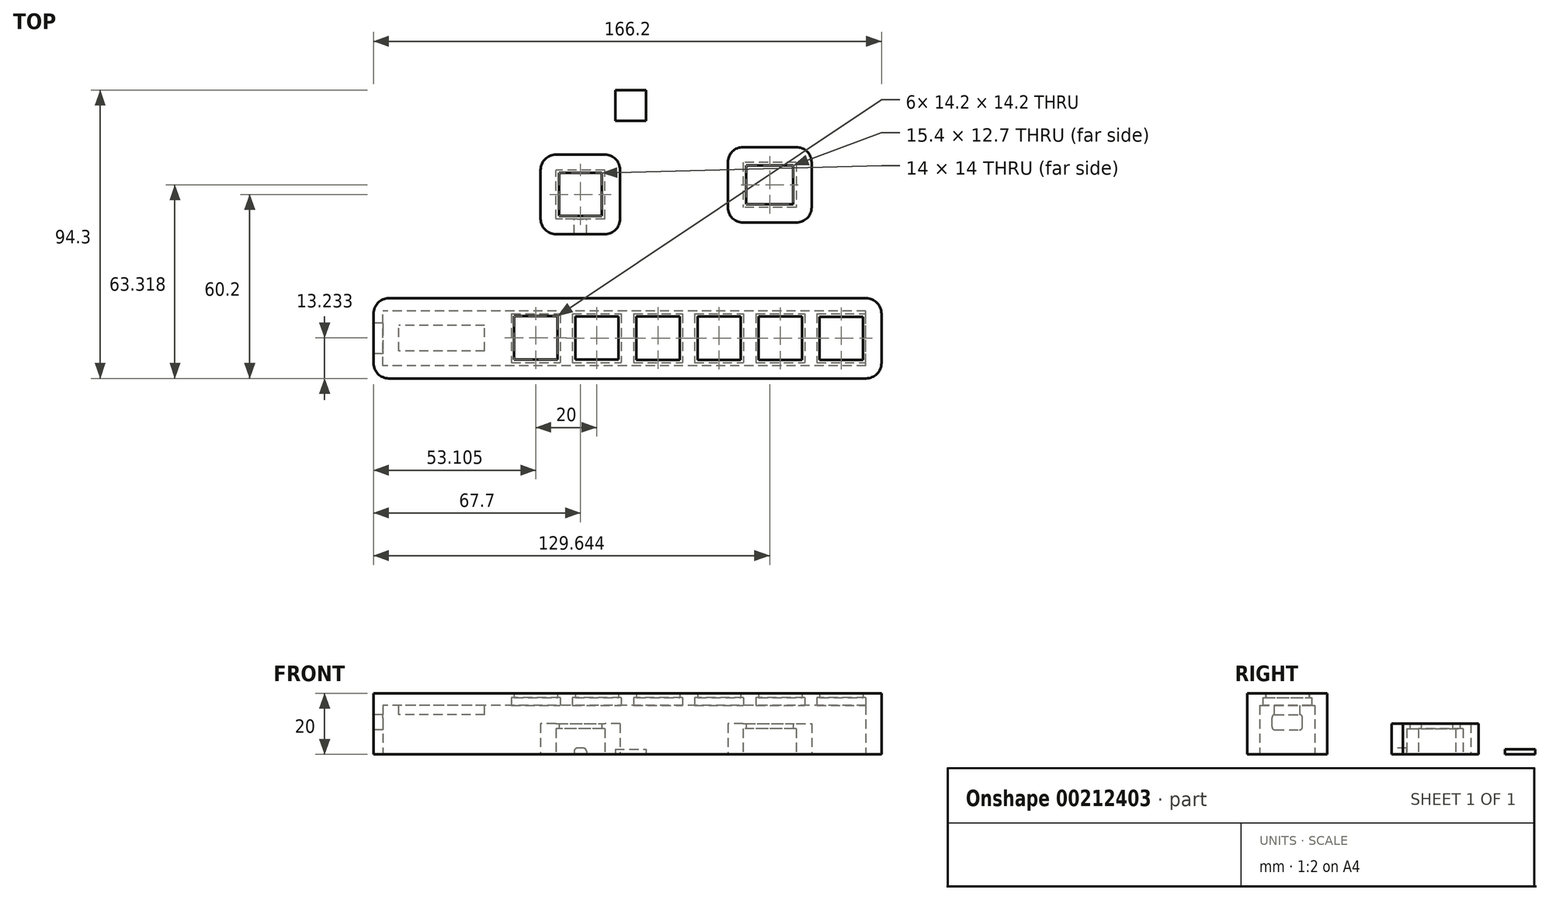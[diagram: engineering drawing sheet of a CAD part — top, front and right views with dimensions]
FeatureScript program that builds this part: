
annotation { "Feature Type Name" : "Feature", "Feature Type Description" : "" }
export const myFeature = defineFeature(function(context is Context, id is Id, definition is map)
    precondition{}
    {
        {
            var Q0;
            Q0=qCreatedBy(makeId("Top.planeOp"),FACE);
            var sketch = newSketch(context, id + "F0", { "sketchPlane" : qUnion([Q0])});
            skLineSegment(sketch, "E0.bottom", {"start": v(-7, 7) * mm, "end": v(7, 7) * mm});
            skLineSegment(sketch, "E0.top", {"start": v(-7, -7) * mm, "end": v(7, -7) * mm});
            skLineSegment(sketch, "E0.left", {"start": v(-7, 7) * mm, "end": v(-7, -7) * mm});
            skLineSegment(sketch, "E0.right", {"start": v(7, 7) * mm, "end": v(7, -7) * mm});
            skLineSegment(sketch, "E1.bottom", {"start": v(-13, 13) * mm, "end": v(13, 13) * mm});
            skLineSegment(sketch, "E1.top", {"start": v(-13, -13) * mm, "end": v(13, -13) * mm});
            skLineSegment(sketch, "E1.left", {"start": v(-13, 13) * mm, "end": v(-13, -13) * mm});
            skLineSegment(sketch, "E1.right", {"start": v(13, 13) * mm, "end": v(13, -13) * mm});
            skLineSegment(sketch, "E2.bottom", {"start": v(54.24, 9.47) * mm, "end": v(69.64, 9.47) * mm});
            skLineSegment(sketch, "E2.top", {"start": v(54.24, -3.23) * mm, "end": v(69.64, -3.23) * mm});
            skLineSegment(sketch, "E2.left", {"start": v(54.24, 9.47) * mm, "end": v(54.24, -3.23) * mm});
            skLineSegment(sketch, "E2.right", {"start": v(69.64, 9.47) * mm, "end": v(69.64, -3.23) * mm});
            skLineSegment(sketch, "E3.bottom", {"start": v(48.24, 15.47) * mm, "end": v(75.64, 15.47) * mm});
            skLineSegment(sketch, "E3.top", {"start": v(48.24, -9.23) * mm, "end": v(75.64, -9.23) * mm});
            skLineSegment(sketch, "E3.left", {"start": v(48.24, 15.47) * mm, "end": v(48.24, -9.23) * mm});
            skLineSegment(sketch, "E3.right", {"start": v(75.64, 15.47) * mm, "end": v(75.64, -9.23) * mm});
            skSolve(sketch);
        }
        {
            var Q0;
            Q0 = qSketchRegion(id + "F0", true);
            extrude(context, id + "F1", {"entities" : qUnion([Q0]), "depth" : 10 * mm});
        }
        {
            var Q0;
            Q0=makeQuery(id+"F1.opExtrude","CAP_FACE",FACE,{"disambiguationData":[OSD([sQuery(id+"F0.wireOp",EDGE,"E0.bottom"),sQuery(id+"F0.wireOp",EDGE,"E0.top"),sQuery(id+"F0.wireOp",EDGE,"E0.left"),sQuery(id+"F0.wireOp",EDGE,"E0.right"),sQuery(id+"F0.wireOp",EDGE,"E1.bottom"),sQuery(id+"F0.wireOp",EDGE,"E1.top"),sQuery(id+"F0.wireOp",EDGE,"E1.left"),sQuery(id+"F0.wireOp",EDGE,"E1.right")])],"isStart":true});
            var sketch = newSketch(context, id + "F2", { "sketchPlane" : qUnion([Q0])});
            skLineSegment(sketch, "E4.bottom", {"start": v(8, 8) * mm, "end": v(-8, 8) * mm});
            skLineSegment(sketch, "E4.top", {"start": v(8, -8) * mm, "end": v(-8, -8) * mm});
            skLineSegment(sketch, "E4.left", {"start": v(8, 8) * mm, "end": v(8, -8) * mm});
            skLineSegment(sketch, "E4.right", {"start": v(-8, 8) * mm, "end": v(-8, -8) * mm});
            skPoint(sketch, "E4.middle", {"position": v(0, 0) * mm});
            skLineSegment(sketch, "E5.bottom", {"start": v(70.64, -10.47) * mm, "end": v(53.24, -10.47) * mm});
            skLineSegment(sketch, "E5.top", {"start": v(70.64, 4.23) * mm, "end": v(53.24, 4.23) * mm});
            skLineSegment(sketch, "E5.left", {"start": v(70.64, -10.47) * mm, "end": v(70.64, 4.23) * mm});
            skLineSegment(sketch, "E5.right", {"start": v(53.24, -10.47) * mm, "end": v(53.24, 4.23) * mm});
            skSolve(sketch);
        }
        {
            var Q0;
            Q0 = qSketchRegion(id + "F2", true);
            extrude(context, id + "F3", {"entities" : qUnion([Q0]), "operationType" : NewBodyOperationType.REMOVE, "oppositeDirection" : true, "depth" : 8.4 * mm});
        }
        {
            var Q0;
            Q0=makeQuery(id+"F1.opExtrude","SWEPT_FACE",FACE,{"disambiguationData":[OSD([sQuery(id+"F0.wireOp",EDGE,"E1.top")])]});
            var sketch = newSketch(context, id + "F4", { "sketchPlane" : qUnion([Q0])});
            skLineSegment(sketch, "E6.bottom", {"start": v(2, 2) * mm, "end": v(-2, 2) * mm});
            skLineSegment(sketch, "E6.top", {"start": v(2, -2) * mm, "end": v(-2, -2) * mm});
            skLineSegment(sketch, "E6.left", {"start": v(2, 2) * mm, "end": v(2, -2) * mm});
            skLineSegment(sketch, "E6.right", {"start": v(-2, 2) * mm, "end": v(-2, -2) * mm});
            skPoint(sketch, "E6.middle", {"position": v(0, 0) * mm});
            skSolve(sketch);
        }
        {
            var Q0;
            Q0 = qSketchRegion(id + "F4", true);
            extrude(context, id + "F5", {"entities" : qUnion([Q0]), "operationType" : NewBodyOperationType.REMOVE, "endBound" : BoundingType.UP_TO_NEXT, "oppositeDirection" : true, "depth" : 25 * mm});
        }
        {
            var Q0;
            Q0=qCreatedBy(makeId("Top.planeOp"),FACE);
            var sketch = newSketch(context, id + "F6", { "sketchPlane" : qUnion([Q0])});
            skLineSegment(sketch, "E7.bottom", {"start": v(-67.7, -34) * mm, "end": v(98.5, -34) * mm});
            skLineSegment(sketch, "E7.top", {"start": v(-67.7, -60.2) * mm, "end": v(98.5, -60.2) * mm});
            skLineSegment(sketch, "E7.left", {"start": v(-67.7, -34) * mm, "end": v(-67.7, -60.2) * mm});
            skLineSegment(sketch, "E7.right", {"start": v(98.5, -34) * mm, "end": v(98.5, -60.2) * mm});
            skLineSegment(sketch, "E8", {"start": v(-67.7, -47.1) * mm, "end": v(98.5, -47.1) * mm, "construction": true});
            skLineSegment(sketch, "E9.bottom", {"start": v(92.5, -40) * mm, "end": v(78.3, -40) * mm});
            skLineSegment(sketch, "E9.top", {"start": v(92.5, -54.2) * mm, "end": v(78.3, -54.2) * mm});
            skLineSegment(sketch, "E9.left", {"start": v(92.5, -40) * mm, "end": v(92.5, -54.2) * mm});
            skLineSegment(sketch, "E9.right", {"start": v(78.3, -40) * mm, "end": v(78.3, -54.2) * mm});
            skPoint(sketch, "E9.middle", {"position": v(85.4, -47.1) * mm});
            skLineSegment(sketch, "E10.1.0.0", {"start": v(58.3, -39.98) * mm, "end": v(58.3, -54.18) * mm});
            skLineSegment(sketch, "E10.1.0.1", {"start": v(72.5, -39.98) * mm, "end": v(72.5, -54.18) * mm});
            skLineSegment(sketch, "E10.1.0.2", {"start": v(72.5, -54.18) * mm, "end": v(58.3, -54.18) * mm});
            skLineSegment(sketch, "E10.1.0.3", {"start": v(72.5, -39.98) * mm, "end": v(58.3, -39.98) * mm});
            skPoint(sketch, "E10.1.0.4", {"position": v(65.4, -47.08) * mm});
            skLineSegment(sketch, "E10.2.0.0", {"start": v(38.3, -39.95) * mm, "end": v(38.3, -54.15) * mm});
            skLineSegment(sketch, "E10.2.0.1", {"start": v(52.5, -39.95) * mm, "end": v(52.5, -54.15) * mm});
            skLineSegment(sketch, "E10.2.0.2", {"start": v(52.5, -54.15) * mm, "end": v(38.3, -54.15) * mm});
            skLineSegment(sketch, "E10.2.0.3", {"start": v(52.5, -39.95) * mm, "end": v(38.3, -39.95) * mm});
            skPoint(sketch, "E10.2.0.4", {"position": v(45.4, -47.05) * mm});
            skLineSegment(sketch, "E10.3.0.0", {"start": v(18.3, -39.92) * mm, "end": v(18.3, -54.12) * mm});
            skLineSegment(sketch, "E10.3.0.1", {"start": v(32.5, -39.92) * mm, "end": v(32.5, -54.12) * mm});
            skLineSegment(sketch, "E10.3.0.2", {"start": v(32.5, -54.12) * mm, "end": v(18.3, -54.12) * mm});
            skLineSegment(sketch, "E10.3.0.3", {"start": v(32.5, -39.92) * mm, "end": v(18.3, -39.92) * mm});
            skPoint(sketch, "E10.3.0.4", {"position": v(25.4, -47.02) * mm});
            skLineSegment(sketch, "E10.4.0.0", {"start": v(-1.7, -39.9) * mm, "end": v(-1.7, -54.1) * mm});
            skLineSegment(sketch, "E10.4.0.1", {"start": v(12.5, -39.9) * mm, "end": v(12.5, -54.1) * mm});
            skLineSegment(sketch, "E10.4.0.2", {"start": v(12.5, -54.1) * mm, "end": v(-1.7, -54.1) * mm});
            skLineSegment(sketch, "E10.4.0.3", {"start": v(12.5, -39.9) * mm, "end": v(-1.7, -39.9) * mm});
            skPoint(sketch, "E10.4.0.4", {"position": v(5.4, -47) * mm});
            skLineSegment(sketch, "E10.5.0.0", {"start": v(-21.7, -39.87) * mm, "end": v(-21.7, -54.07) * mm});
            skLineSegment(sketch, "E10.5.0.1", {"start": v(-7.5, -39.87) * mm, "end": v(-7.5, -54.07) * mm});
            skLineSegment(sketch, "E10.5.0.2", {"start": v(-7.5, -54.07) * mm, "end": v(-21.7, -54.07) * mm});
            skLineSegment(sketch, "E10.5.0.3", {"start": v(-7.5, -39.87) * mm, "end": v(-21.7, -39.87) * mm});
            skPoint(sketch, "E10.5.0.4", {"position": v(-14.6, -46.97) * mm});
            skLineSegment(sketch, "E10.direction1", {"start": v(78.3, -54.2) * mm, "end": v(58.3, -54.18) * mm, "construction": true});
            skSolve(sketch);
        }
        {
            var Q0;
            Q0 = qSketchRegion(id + "F6", true);
            extrude(context, id + "F7", {"entities" : qUnion([Q0]), "depth" : 20 * mm});
        }
        {
            var Q0;
            Q0=makeQuery(id+"F7.opExtrude","CAP_FACE",FACE,{"disambiguationData":[OSD([sQuery(id+"F6.wireOp",EDGE,"E7.bottom"),sQuery(id+"F6.wireOp",EDGE,"E7.top"),sQuery(id+"F6.wireOp",EDGE,"E7.left"),sQuery(id+"F6.wireOp",EDGE,"E7.right"),sQuery(id+"F6.wireOp",EDGE,"E9.bottom"),sQuery(id+"F6.wireOp",EDGE,"E9.top"),sQuery(id+"F6.wireOp",EDGE,"E9.left"),sQuery(id+"F6.wireOp",EDGE,"E9.right"),sQuery(id+"F6.wireOp",EDGE,"E10.1.0.0"),sQuery(id+"F6.wireOp",EDGE,"E10.1.0.1"),sQuery(id+"F6.wireOp",EDGE,"E10.1.0.2"),sQuery(id+"F6.wireOp",EDGE,"E10.1.0.3"),sQuery(id+"F6.wireOp",EDGE,"E10.2.0.0"),sQuery(id+"F6.wireOp",EDGE,"E10.2.0.1"),sQuery(id+"F6.wireOp",EDGE,"E10.2.0.2"),sQuery(id+"F6.wireOp",EDGE,"E10.2.0.3"),sQuery(id+"F6.wireOp",EDGE,"E10.3.0.0"),sQuery(id+"F6.wireOp",EDGE,"E10.3.0.1"),sQuery(id+"F6.wireOp",EDGE,"E10.3.0.2"),sQuery(id+"F6.wireOp",EDGE,"E10.3.0.3"),sQuery(id+"F6.wireOp",EDGE,"E10.4.0.0"),sQuery(id+"F6.wireOp",EDGE,"E10.4.0.1"),sQuery(id+"F6.wireOp",EDGE,"E10.4.0.2"),sQuery(id+"F6.wireOp",EDGE,"E10.4.0.3"),sQuery(id+"F6.wireOp",EDGE,"E10.5.0.0"),sQuery(id+"F6.wireOp",EDGE,"E10.5.0.1"),sQuery(id+"F6.wireOp",EDGE,"E10.5.0.2"),sQuery(id+"F6.wireOp",EDGE,"E10.5.0.3")])],"isStart":true});
            var sketch = newSketch(context, id + "F8", { "sketchPlane" : qUnion([Q0])});
            skLineSegment(sketch, "E11.bottom", {"start": v(93.4, 55.1) * mm, "end": v(77.4, 55.1) * mm});
            skLineSegment(sketch, "E11.top", {"start": v(93.4, 39.1) * mm, "end": v(77.4, 39.1) * mm});
            skLineSegment(sketch, "E11.left", {"start": v(93.4, 55.1) * mm, "end": v(93.4, 39.1) * mm});
            skLineSegment(sketch, "E11.right", {"start": v(77.4, 55.1) * mm, "end": v(77.4, 39.1) * mm});
            skPoint(sketch, "E11.middle", {"position": v(85.4, 47.1) * mm});
            skPoint(sketch, "E11.middle.positionSnap0", {"position": v(85.4, 40) * mm});
            skPoint(sketch, "E11.middle.positionSnap1", {"position": v(92.5, 47.1) * mm});
            skPoint(sketch, "E11.centerSnap0", {"position": v(85.4, 40) * mm});
            skPoint(sketch, "E11.centerSnap1", {"position": v(92.5, 47.1) * mm});
            skPoint(sketch, "E12.1.0.0", {"position": v(65.4, 40) * mm});
            skPoint(sketch, "E12.1.0.1", {"position": v(72.5, 47.1) * mm});
            skPoint(sketch, "E12.1.0.2", {"position": v(65.4, 47.1) * mm});
            skLineSegment(sketch, "E12.1.0.3", {"start": v(57.4, 55.1) * mm, "end": v(57.4, 39.1) * mm});
            skLineSegment(sketch, "E12.1.0.4", {"start": v(73.4, 55.1) * mm, "end": v(73.4, 39.1) * mm});
            skLineSegment(sketch, "E12.1.0.5", {"start": v(73.4, 39.1) * mm, "end": v(57.4, 39.1) * mm});
            skLineSegment(sketch, "E12.1.0.6", {"start": v(73.4, 55.1) * mm, "end": v(57.4, 55.1) * mm});
            skPoint(sketch, "E12.1.0.7", {"position": v(72.5, 47.1) * mm});
            skPoint(sketch, "E12.1.0.8", {"position": v(65.4, 40) * mm});
            skPoint(sketch, "E12.2.0.0", {"position": v(45.4, 40) * mm});
            skPoint(sketch, "E12.2.0.1", {"position": v(52.5, 47.1) * mm});
            skPoint(sketch, "E12.2.0.2", {"position": v(45.4, 47.1) * mm});
            skLineSegment(sketch, "E12.2.0.3", {"start": v(37.4, 55.1) * mm, "end": v(37.4, 39.1) * mm});
            skLineSegment(sketch, "E12.2.0.4", {"start": v(53.4, 55.1) * mm, "end": v(53.4, 39.1) * mm});
            skLineSegment(sketch, "E12.2.0.5", {"start": v(53.4, 39.1) * mm, "end": v(37.4, 39.1) * mm});
            skLineSegment(sketch, "E12.2.0.6", {"start": v(53.4, 55.1) * mm, "end": v(37.4, 55.1) * mm});
            skPoint(sketch, "E12.2.0.7", {"position": v(52.5, 47.1) * mm});
            skPoint(sketch, "E12.2.0.8", {"position": v(45.4, 40) * mm});
            skPoint(sketch, "E12.3.0.0", {"position": v(25.4, 40) * mm});
            skPoint(sketch, "E12.3.0.1", {"position": v(32.5, 47.1) * mm});
            skPoint(sketch, "E12.3.0.2", {"position": v(25.4, 47.1) * mm});
            skLineSegment(sketch, "E12.3.0.3", {"start": v(17.4, 55.1) * mm, "end": v(17.4, 39.1) * mm});
            skLineSegment(sketch, "E12.3.0.4", {"start": v(33.4, 55.1) * mm, "end": v(33.4, 39.1) * mm});
            skLineSegment(sketch, "E12.3.0.5", {"start": v(33.4, 39.1) * mm, "end": v(17.4, 39.1) * mm});
            skLineSegment(sketch, "E12.3.0.6", {"start": v(33.4, 55.1) * mm, "end": v(17.4, 55.1) * mm});
            skPoint(sketch, "E12.3.0.7", {"position": v(32.5, 47.1) * mm});
            skPoint(sketch, "E12.3.0.8", {"position": v(25.4, 40) * mm});
            skPoint(sketch, "E12.4.0.0", {"position": v(5.4, 40) * mm});
            skPoint(sketch, "E12.4.0.1", {"position": v(12.5, 47.1) * mm});
            skPoint(sketch, "E12.4.0.2", {"position": v(5.4, 47.1) * mm});
            skLineSegment(sketch, "E12.4.0.3", {"start": v(-2.6, 55.1) * mm, "end": v(-2.6, 39.1) * mm});
            skLineSegment(sketch, "E12.4.0.4", {"start": v(13.4, 55.1) * mm, "end": v(13.4, 39.1) * mm});
            skLineSegment(sketch, "E12.4.0.5", {"start": v(13.4, 39.1) * mm, "end": v(-2.6, 39.1) * mm});
            skLineSegment(sketch, "E12.4.0.6", {"start": v(13.4, 55.1) * mm, "end": v(-2.6, 55.1) * mm});
            skPoint(sketch, "E12.4.0.7", {"position": v(12.5, 47.1) * mm});
            skPoint(sketch, "E12.4.0.8", {"position": v(5.4, 40) * mm});
            skPoint(sketch, "E12.5.0.0", {"position": v(-14.6, 40) * mm});
            skPoint(sketch, "E12.5.0.1", {"position": v(-7.5, 47.1) * mm});
            skPoint(sketch, "E12.5.0.2", {"position": v(-14.6, 47.1) * mm});
            skLineSegment(sketch, "E12.5.0.3", {"start": v(-22.6, 55.1) * mm, "end": v(-22.6, 39.1) * mm});
            skLineSegment(sketch, "E12.5.0.4", {"start": v(-6.6, 55.1) * mm, "end": v(-6.6, 39.1) * mm});
            skLineSegment(sketch, "E12.5.0.5", {"start": v(-6.6, 39.1) * mm, "end": v(-22.6, 39.1) * mm});
            skLineSegment(sketch, "E12.5.0.6", {"start": v(-6.6, 55.1) * mm, "end": v(-22.6, 55.1) * mm});
            skPoint(sketch, "E12.5.0.7", {"position": v(-7.5, 47.1) * mm});
            skPoint(sketch, "E12.5.0.8", {"position": v(-14.6, 40) * mm});
            skLineSegment(sketch, "E12.direction1", {"start": v(77.4, 39.1) * mm, "end": v(57.4, 39.1) * mm, "construction": true});
            skSolve(sketch);
        }
        {
            var Q0;
            Q0 = qSketchRegion(id + "F8", true);
            extrude(context, id + "F9", {"entities" : qUnion([Q0]), "operationType" : NewBodyOperationType.REMOVE, "oppositeDirection" : true, "depth" : 18.5 * mm});
        }
        {
            var Q0;
            Q0=makeQuery(id+"F7.opExtrude","CAP_FACE",FACE,{"disambiguationData":[OSD([sQuery(id+"F6.wireOp",EDGE,"E7.bottom"),sQuery(id+"F6.wireOp",EDGE,"E7.top"),sQuery(id+"F6.wireOp",EDGE,"E7.left"),sQuery(id+"F6.wireOp",EDGE,"E7.right"),sQuery(id+"F6.wireOp",EDGE,"E9.bottom"),sQuery(id+"F6.wireOp",EDGE,"E9.top"),sQuery(id+"F6.wireOp",EDGE,"E9.left"),sQuery(id+"F6.wireOp",EDGE,"E9.right"),sQuery(id+"F6.wireOp",EDGE,"E10.1.0.0"),sQuery(id+"F6.wireOp",EDGE,"E10.1.0.1"),sQuery(id+"F6.wireOp",EDGE,"E10.1.0.2"),sQuery(id+"F6.wireOp",EDGE,"E10.1.0.3"),sQuery(id+"F6.wireOp",EDGE,"E10.2.0.0"),sQuery(id+"F6.wireOp",EDGE,"E10.2.0.1"),sQuery(id+"F6.wireOp",EDGE,"E10.2.0.2"),sQuery(id+"F6.wireOp",EDGE,"E10.2.0.3"),sQuery(id+"F6.wireOp",EDGE,"E10.3.0.0"),sQuery(id+"F6.wireOp",EDGE,"E10.3.0.1"),sQuery(id+"F6.wireOp",EDGE,"E10.3.0.2"),sQuery(id+"F6.wireOp",EDGE,"E10.3.0.3"),sQuery(id+"F6.wireOp",EDGE,"E10.4.0.0"),sQuery(id+"F6.wireOp",EDGE,"E10.4.0.1"),sQuery(id+"F6.wireOp",EDGE,"E10.4.0.2"),sQuery(id+"F6.wireOp",EDGE,"E10.4.0.3"),sQuery(id+"F6.wireOp",EDGE,"E10.5.0.0"),sQuery(id+"F6.wireOp",EDGE,"E10.5.0.1"),sQuery(id+"F6.wireOp",EDGE,"E10.5.0.2"),sQuery(id+"F6.wireOp",EDGE,"E10.5.0.3")])],"isStart":true});
            var sketch = newSketch(context, id + "F10", { "sketchPlane" : qUnion([Q0])});
            skLineSegment(sketch, "E13.bottom", {"start": v(93.4, 56.1) * mm, "end": v(-64.7, 56.1) * mm});
            skLineSegment(sketch, "E13.top", {"start": v(93.4, 38.1) * mm, "end": v(-64.7, 38.1) * mm});
            skLineSegment(sketch, "E13.left", {"start": v(93.4, 56.1) * mm, "end": v(93.4, 38.1) * mm});
            skLineSegment(sketch, "E13.right", {"start": v(-64.7, 56.1) * mm, "end": v(-64.7, 38.1) * mm});
            skPoint(sketch, "E13.middle", {"position": v(14.35, 47.1) * mm});
            skPoint(sketch, "E13.middle.positionSnap0", {"position": v(-67.7, 47.1) * mm});
            skPoint(sketch, "E13.centerSnap0", {"position": v(-67.7, 47.1) * mm});
            skSolve(sketch);
        }
        {
            var Q0;
            Q0 = qSketchRegion(id + "F10", true);
            extrude(context, id + "F11", {"entities" : qUnion([Q0]), "operationType" : NewBodyOperationType.REMOVE, "oppositeDirection" : true, "depth" : 16 * mm});
        }
        {
            var Q0;
            Q0=makeQuery(id+"F11.boolean.opBoolean","COPY",FACE,{"derivedFrom":makeQuery(id+"F11.opExtrude","CAP_FACE",FACE,{"disambiguationData":[OSD([sQuery(id+"F10.wireOp",EDGE,"E13.bottom"),sQuery(id+"F10.wireOp",EDGE,"E13.top"),sQuery(id+"F10.wireOp",EDGE,"E13.left"),sQuery(id+"F10.wireOp",EDGE,"E13.right")])],"isStart":false})});
            var sketch = newSketch(context, id + "F12", { "sketchPlane" : qUnion([Q0])});
            skLineSegment(sketch, "E14.bottom", {"start": v(-31.3, 51.3) * mm, "end": v(-59.48, 51.3) * mm});
            skLineSegment(sketch, "E14.top", {"start": v(-31.3, 42.9) * mm, "end": v(-59.48, 42.9) * mm});
            skLineSegment(sketch, "E14.left", {"start": v(-31.3, 51.3) * mm, "end": v(-31.3, 42.9) * mm});
            skLineSegment(sketch, "E14.right", {"start": v(-59.48, 51.3) * mm, "end": v(-59.48, 42.9) * mm});
            skPoint(sketch, "E14.middle", {"position": v(-45.4, 47.1) * mm});
            skPoint(sketch, "E14.middle.positionSnap0", {"position": v(-64.7, 47.1) * mm});
            skPoint(sketch, "E14.centerSnap0", {"position": v(-64.7, 47.1) * mm});
            skSolve(sketch);
        }
        {
            var Q0;
            Q0 = qSketchRegion(id + "F12", true);
            extrude(context, id + "F13", {"entities" : qUnion([Q0]), "operationType" : NewBodyOperationType.ADD, "depth" : 3 * mm});
        }
        {
            var Q0;
            Q0=makeQuery(id+"F7.opExtrude","SWEPT_FACE",FACE,{"disambiguationData":[OSD([sQuery(id+"F6.wireOp",EDGE,"E7.left")])]});
            var sketch = newSketch(context, id + "F14", { "sketchPlane" : qUnion([Q0])});
            skLineSegment(sketch, "E15.bottom", {"start": v(52.1, 8) * mm, "end": v(42.1, 8) * mm});
            skLineSegment(sketch, "E15.top", {"start": v(52.1, 13) * mm, "end": v(42.1, 13) * mm});
            skLineSegment(sketch, "E15.left", {"start": v(52.1, 8) * mm, "end": v(52.1, 13) * mm});
            skLineSegment(sketch, "E15.right", {"start": v(42.1, 8) * mm, "end": v(42.1, 13) * mm});
            skPoint(sketch, "E15.middle", {"position": v(47.1, 10.5) * mm});
            skPoint(sketch, "E15.middle.positionSnap0", {"position": v(47.1, 20) * mm});
            skPoint(sketch, "E15.centerSnap0", {"position": v(47.1, 20) * mm});
            skSolve(sketch);
        }
        {
            var Q0;
            Q0 = qSketchRegion(id + "F14", true);
            extrude(context, id + "F15", {"entities" : qUnion([Q0]), "operationType" : NewBodyOperationType.REMOVE, "endBound" : BoundingType.UP_TO_NEXT, "oppositeDirection" : true, "depth" : 25 * mm});
        }
        {
            var Q0;
            Q0=makeQuery(id+"F1.opExtrude","SWEPT_EDGE",EDGE,{"disambiguationData":[OSD([sQuery(id+"F0.wireOp",EDGE,"E1.top"),sQuery(id+"F0.wireOp",EDGE,"E1.left")])]});
            var Q1;
            Q1=makeQuery(id+"F1.opExtrude","SWEPT_EDGE",EDGE,{"disambiguationData":[OSD([sQuery(id+"F0.wireOp",EDGE,"E1.bottom"),sQuery(id+"F0.wireOp",EDGE,"E1.left")])]});
            var Q2;
            Q2=makeQuery(id+"F1.opExtrude","SWEPT_EDGE",EDGE,{"disambiguationData":[OSD([sQuery(id+"F0.wireOp",EDGE,"E1.top"),sQuery(id+"F0.wireOp",EDGE,"E1.right")])]});
            var Q3;
            Q3=makeQuery(id+"F1.opExtrude","SWEPT_EDGE",EDGE,{"disambiguationData":[OSD([sQuery(id+"F0.wireOp",EDGE,"E1.bottom"),sQuery(id+"F0.wireOp",EDGE,"E1.right")])]});
            var Q4;
            Q4=makeQuery(id+"F7.opExtrude","SWEPT_EDGE",EDGE,{"disambiguationData":[OSD([sQuery(id+"F6.wireOp",EDGE,"E7.bottom"),sQuery(id+"F6.wireOp",EDGE,"E7.left")])]});
            var Q5;
            Q5=makeQuery(id+"F7.opExtrude","SWEPT_EDGE",EDGE,{"disambiguationData":[OSD([sQuery(id+"F6.wireOp",EDGE,"E7.top"),sQuery(id+"F6.wireOp",EDGE,"E7.left")])]});
            var Q6;
            Q6=makeQuery(id+"F7.opExtrude","SWEPT_EDGE",EDGE,{"disambiguationData":[OSD([sQuery(id+"F6.wireOp",EDGE,"E7.top"),sQuery(id+"F6.wireOp",EDGE,"E7.right")])]});
            var Q7;
            Q7=makeQuery(id+"F7.opExtrude","SWEPT_EDGE",EDGE,{"disambiguationData":[OSD([sQuery(id+"F6.wireOp",EDGE,"E7.bottom"),sQuery(id+"F6.wireOp",EDGE,"E7.right")])]});
            var Q8;
            Q8=makeQuery(id+"F1.opExtrude","SWEPT_EDGE",EDGE,{"disambiguationData":[OSD([sQuery(id+"F0.wireOp",EDGE,"E3.bottom"),sQuery(id+"F0.wireOp",EDGE,"E3.right")])]});
            var Q9;
            Q9=makeQuery(id+"F1.opExtrude","SWEPT_EDGE",EDGE,{"disambiguationData":[OSD([sQuery(id+"F0.wireOp",EDGE,"E3.top"),sQuery(id+"F0.wireOp",EDGE,"E3.right")])]});
            var Q10;
            Q10=makeQuery(id+"F1.opExtrude","SWEPT_EDGE",EDGE,{"disambiguationData":[OSD([sQuery(id+"F0.wireOp",EDGE,"E3.top"),sQuery(id+"F0.wireOp",EDGE,"E3.left")])]});
            var Q11;
            Q11=makeQuery(id+"F1.opExtrude","SWEPT_EDGE",EDGE,{"disambiguationData":[OSD([sQuery(id+"F0.wireOp",EDGE,"E3.bottom"),sQuery(id+"F0.wireOp",EDGE,"E3.left")])]});
            fillet(context, id + "F16", {"entities" : qUnion([Q0, Q1, Q2, Q3, Q4, Q5, Q6, Q7, Q8, Q9, Q10, Q11]), "radius" : 5 * mm, "tangentPropagation" : true, "allowEdgeOverflow" : false});
        }
        {
            var Q0;
            Q0=makeQuery(id+"F5.boolean.opBoolean","COPY",EDGE,{"derivedFrom":makeQuery(id+"F5.opExtrude","SWEPT_EDGE",EDGE,{"disambiguationData":[OSD([sQuery(id+"F4.wireOp",EDGE,"E6.bottom"),sQuery(id+"F4.wireOp",EDGE,"E6.right")])]})});
            var Q1;
            Q1=makeQuery(id+"F5.boolean.opBoolean","COPY",EDGE,{"derivedFrom":makeQuery(id+"F5.opExtrude","SWEPT_EDGE",EDGE,{"disambiguationData":[OSD([sQuery(id+"F4.wireOp",EDGE,"E6.bottom"),sQuery(id+"F4.wireOp",EDGE,"E6.left")])]})});
            var Q2;
            Q2=makeQuery(id+"F15.boolean.opBoolean","COPY",EDGE,{"derivedFrom":makeQuery(id+"F15.opExtrude","SWEPT_EDGE",EDGE,{"disambiguationData":[OSD([sQuery(id+"F14.wireOp",EDGE,"E15.top"),sQuery(id+"F14.wireOp",EDGE,"E15.right")])]})});
            var Q3;
            Q3=makeQuery(id+"F15.boolean.opBoolean","COPY",EDGE,{"derivedFrom":makeQuery(id+"F15.opExtrude","SWEPT_EDGE",EDGE,{"disambiguationData":[OSD([sQuery(id+"F14.wireOp",EDGE,"E15.top"),sQuery(id+"F14.wireOp",EDGE,"E15.left")])]})});
            var Q4;
            Q4=makeQuery(id+"F15.boolean.opBoolean","COPY",EDGE,{"derivedFrom":makeQuery(id+"F15.opExtrude","SWEPT_EDGE",EDGE,{"disambiguationData":[OSD([sQuery(id+"F14.wireOp",EDGE,"E15.bottom"),sQuery(id+"F14.wireOp",EDGE,"E15.right")])]})});
            var Q5;
            Q5=makeQuery(id+"F15.boolean.opBoolean","COPY",EDGE,{"derivedFrom":makeQuery(id+"F15.opExtrude","SWEPT_EDGE",EDGE,{"disambiguationData":[OSD([sQuery(id+"F14.wireOp",EDGE,"E15.bottom"),sQuery(id+"F14.wireOp",EDGE,"E15.left")])]})});
            fillet(context, id + "F17", {"entities" : qUnion([Q0, Q1, Q2, Q3, Q4, Q5]), "radius" : 1 * mm, "tangentPropagation" : true, "allowEdgeOverflow" : false});
        }
        {
            var Q0;
            Q0=qCreatedBy(makeId("Top.planeOp"),FACE);
            var sketch = newSketch(context, id + "F18", { "sketchPlane" : qUnion([Q0])});
            skLineSegment(sketch, "E16.bottom", {"start": v(11.42, 34.1) * mm, "end": v(21.42, 34.1) * mm});
            skLineSegment(sketch, "E16.top", {"start": v(11.42, 24.1) * mm, "end": v(21.42, 24.1) * mm});
            skLineSegment(sketch, "E16.left", {"start": v(11.42, 34.1) * mm, "end": v(11.42, 24.1) * mm});
            skLineSegment(sketch, "E16.right", {"start": v(21.42, 34.1) * mm, "end": v(21.42, 24.1) * mm});
            skSolve(sketch);
        }
        {
            var Q0;
            Q0 = qSketchRegion(id + "F18", true);
            extrude(context, id + "F19", {"entities" : qUnion([Q0]), "depth" : 1.6 * mm});
        }
    });
